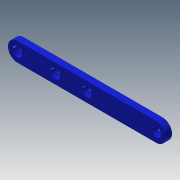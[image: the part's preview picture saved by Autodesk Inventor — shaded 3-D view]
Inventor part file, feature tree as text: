
AUTODESK INVENTOR PART (.ipt)
format: ipt  version: 2013 (Build 170138000, 138)  size: 104,448 bytes
history: native  units: mm
features: extrude x3, sketch x3
ambient origin geometry x8: Origin, YZ Plane, XZ Plane, XY Plane, X Axis, Y Axis, Z Axis, Center Point
bodies: Solid1 (feature_tree)
feature tree (6):
  extrude  "Extrusion1"  Depth=6.0mm
  extrude  "Extrusion2"  Depth=6.0mm
  extrude  "Extrusion3"  Depth=3.0mm
  sketch  "Sketch1"  dims[d0=44.0mm d1=6.0mm]
  sketch  "Sketch2"  dims[d2=6.0mm d3=6.0mm]
  sketch  "Sketch3"  dims[d4=2.0mm d5=0.0mm d6=3.0mm d7=3.0mm d8=3.0mm d9=2.0mm d10=0.0mm d11=10.0mm d12=3.0mm d13=2.0mm d14=0.0mm]
